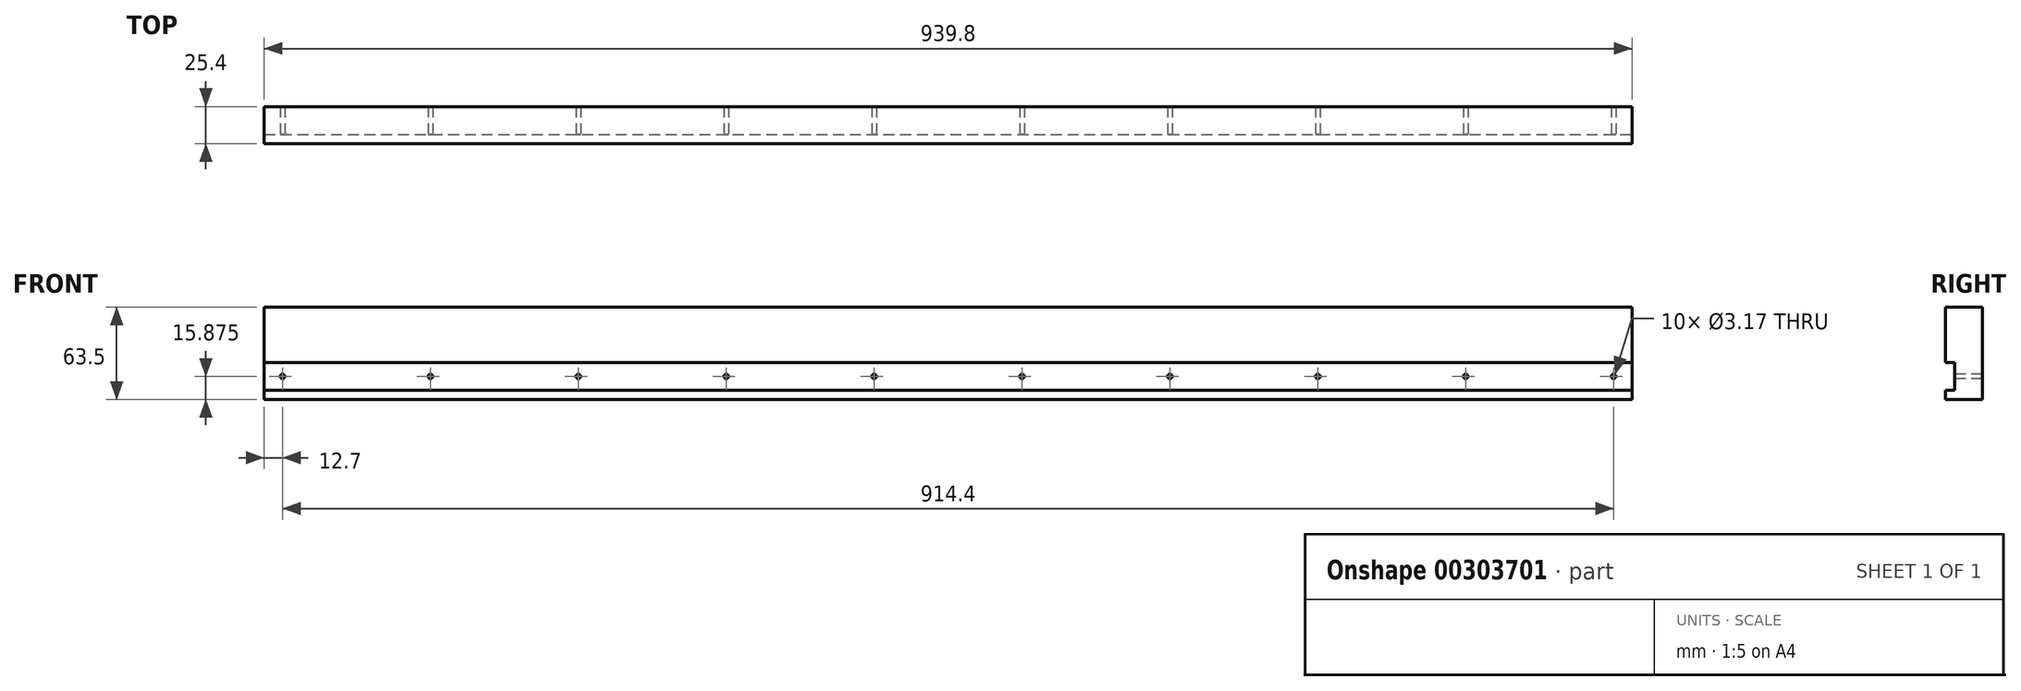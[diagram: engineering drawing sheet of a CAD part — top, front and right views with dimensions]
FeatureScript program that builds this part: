
annotation { "Feature Type Name" : "Feature", "Feature Type Description" : "" }
export const myFeature = defineFeature(function(context is Context, id is Id, definition is map)
    precondition{}
    {
        {
            var Q0;
            Q0=qCreatedBy(makeId("Front.planeOp"),FACE);
            var sketch = newSketch(context, id + "F0", { "sketchPlane" : qUnion([Q0])});
            skLineSegment(sketch, "E0.bottom", {"start": v(0, 0) * mm, "end": v(939.8, 0) * mm});
            skLineSegment(sketch, "E0.top", {"start": v(0, -63.5) * mm, "end": v(939.8, -63.5) * mm});
            skLineSegment(sketch, "E0.left", {"start": v(0, 0) * mm, "end": v(0, -63.5) * mm});
            skLineSegment(sketch, "E0.right", {"start": v(939.8, 0) * mm, "end": v(939.8, -63.5) * mm});
            skSolve(sketch);
        }
        {
            var Q0;
            Q0 = qSketchRegion(id + "F0", true);
            extrude(context, id + "F1", {"entities" : qUnion([Q0]), "oppositeDirection" : true, "depth" : 25.4 * mm});
        }
        {
            var Q0;
            Q0=qCreatedBy(makeId("Front.planeOp"),FACE);
            var sketch = newSketch(context, id + "F2", { "sketchPlane" : qUnion([Q0])});
            skLineSegment(sketch, "E1.bottom", {"start": v(0, -38.1) * mm, "end": v(939.8, -38.1) * mm});
            skLineSegment(sketch, "E1.top", {"start": v(0, -57.15) * mm, "end": v(939.8, -57.15) * mm});
            skLineSegment(sketch, "E1.left", {"start": v(0, -38.1) * mm, "end": v(0, -57.15) * mm});
            skLineSegment(sketch, "E1.right", {"start": v(939.8, -38.1) * mm, "end": v(939.8, -57.15) * mm});
            skSolve(sketch);
        }
        {
            var Q0;
            Q0 = qSketchRegion(id + "F2", true);
            extrude(context, id + "F3", {"entities" : qUnion([Q0]), "operationType" : NewBodyOperationType.REMOVE, "oppositeDirection" : true, "depth" : 6.35 * mm});
        }
        {
            var Q0;
            Q0=qCreatedBy(makeId("Front.planeOp"),FACE);
            var sketch = newSketch(context, id + "F4", { "sketchPlane" : qUnion([Q0])});
            skCircle(sketch, "E2", {"center": v(12.7, -47.62) * mm, "radius": 1.59 * mm});
            skCircle(sketch, "E3.1.0.0", {"center": v(114.3, -47.62) * mm, "radius": 1.59 * mm});
            skCircle(sketch, "E3.2.0.0", {"center": v(215.9, -47.62) * mm, "radius": 1.59 * mm});
            skCircle(sketch, "E3.3.0.0", {"center": v(317.5, -47.62) * mm, "radius": 1.59 * mm});
            skCircle(sketch, "E3.4.0.0", {"center": v(419.1, -47.62) * mm, "radius": 1.59 * mm});
            skCircle(sketch, "E3.5.0.0", {"center": v(520.7, -47.62) * mm, "radius": 1.59 * mm});
            skCircle(sketch, "E3.6.0.0", {"center": v(622.3, -47.62) * mm, "radius": 1.59 * mm});
            skCircle(sketch, "E3.7.0.0", {"center": v(723.9, -47.62) * mm, "radius": 1.59 * mm});
            skCircle(sketch, "E3.8.0.0", {"center": v(825.5, -47.62) * mm, "radius": 1.59 * mm});
            skCircle(sketch, "E3.9.0.0", {"center": v(927.1, -47.62) * mm, "radius": 1.59 * mm});
            skLineSegment(sketch, "E3.direction1", {"start": v(19.05, -47.62) * mm, "end": v(120.65, -47.62) * mm, "construction": true});
            skSolve(sketch);
        }
        {
            var Q0;
            Q0 = qSketchRegion(id + "F4", true);
            extrude(context, id + "F5", {"entities" : qUnion([Q0]), "operationType" : NewBodyOperationType.REMOVE, "endBound" : BoundingType.THROUGH_ALL, "oppositeDirection" : true, "depth" : 25.4 * mm});
        }
    });
